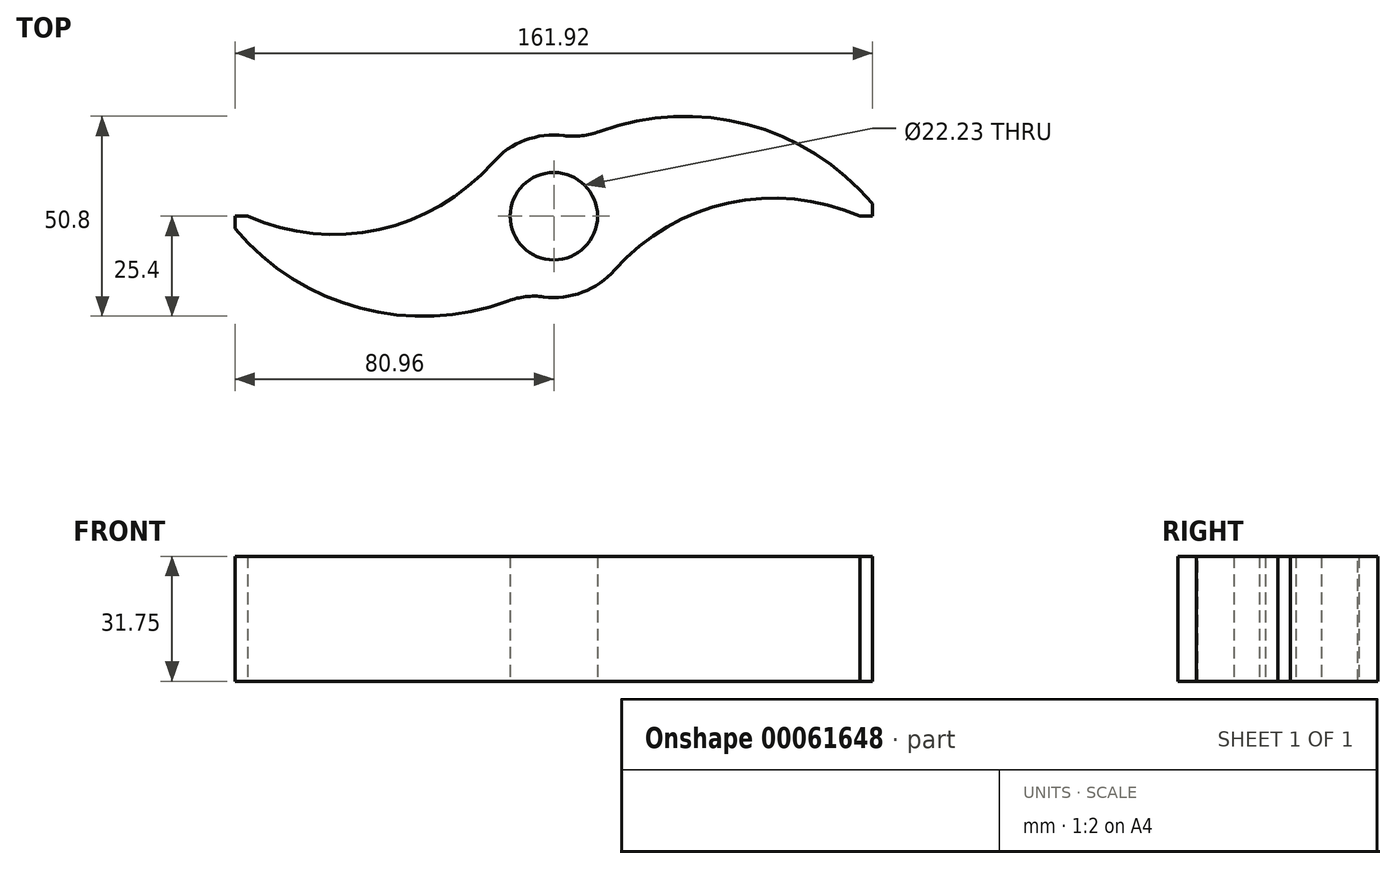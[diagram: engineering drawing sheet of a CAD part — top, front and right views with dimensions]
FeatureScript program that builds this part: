
annotation { "Feature Type Name" : "Feature", "Feature Type Description" : "" }
export const myFeature = defineFeature(function(context is Context, id is Id, definition is map)
    precondition{}
    {
        {
            var Q0;
            Q0=qCreatedBy(makeId("Top.planeOp"),FACE);
            var sketch = newSketch(context, id + "F0", { "sketchPlane" : qUnion([Q0])});
            skCircle(sketch, "E0", {"center": v(0, 0) * mm, "radius": 20.64 * mm});
            skLineSegment(sketch, "E1", {"start": v(0, 0) * mm, "end": v(80.96, 0) * mm, "construction": true});
            skLineSegment(sketch, "E2", {"start": v(0, 0) * mm, "end": v(-80.96, 0) * mm, "construction": true});
            skLineSegment(sketch, "E3.bottom", {"start": v(-80.96, 0) * mm, "end": v(-77.79, 0) * mm});
            skLineSegment(sketch, "E3.top", {"start": v(-80.96, -3.18) * mm, "end": v(-77.79, -3.18) * mm});
            skLineSegment(sketch, "E3.left", {"start": v(-80.96, 0) * mm, "end": v(-80.96, -3.18) * mm});
            skLineSegment(sketch, "E3.right", {"start": v(-77.79, 0) * mm, "end": v(-77.79, -3.18) * mm});
            skLineSegment(sketch, "E4.bottom", {"start": v(80.96, 0) * mm, "end": v(77.79, 0) * mm});
            skLineSegment(sketch, "E4.top", {"start": v(80.96, 3.18) * mm, "end": v(77.79, 3.17) * mm});
            skLineSegment(sketch, "E4.left", {"start": v(80.96, 0) * mm, "end": v(80.96, 3.18) * mm});
            skLineSegment(sketch, "E4.right", {"start": v(77.79, 0) * mm, "end": v(77.79, 3.17) * mm});
            skLineSegment(sketch, "E5", {"start": v(0, 25.4) * mm, "end": v(76.2, 25.4) * mm, "construction": true});
            skLineSegment(sketch, "E6", {"start": v(0, -25.4) * mm, "end": v(-76.2, -25.4) * mm, "construction": true});
            skArc(sketch, "E7", {"start": v(80.96, 3.17) * mm, "mid": v(46.64, 23.95) * mm, "end": v(6.78, 19.5) * mm});
            skArc(sketch, "E8", {"start": v(-80.96, -3.18) * mm, "mid": v(-46.64, -23.95) * mm, "end": v(-6.78, -19.5) * mm});
            skArc(sketch, "E9", {"start": v(-77.79, 0) * mm, "mid": v(-44.4, -3.36) * mm, "end": v(-15.48, 13.65) * mm});
            skArc(sketch, "E10", {"start": v(77.79, 0) * mm, "mid": v(44.4, 3.36) * mm, "end": v(15.48, -13.65) * mm});
            skSolve(sketch);
        }
        {
            var Q0;
            Q0 = qSketchRegion(id + "F0", true);
            extrude(context, id + "F1", {"entities" : qUnion([Q0]), "depth" : 31.75 * mm});
        }
        {
            var Q0;
            Q0=qCreatedBy(makeId("Top.planeOp"),FACE);
            var sketch = newSketch(context, id + "F2", { "sketchPlane" : qUnion([Q0])});
            skCircle(sketch, "E11", {"center": v(0, 0) * mm, "radius": 11.11 * mm});
            skSolve(sketch);
        }
        {
            var Q0;
            Q0 = qSketchRegion(id + "F2", true);
            extrude(context, id + "F3", {"entities" : qUnion([Q0]), "operationType" : NewBodyOperationType.REMOVE, "depth" : 31.75 * mm});
        }
        {
            var Q0;
            Q0=makeQuery(id+"F1.opExtrude","SWEPT_EDGE",EDGE,{"disambiguationData":[OSD([sQuery(id+"F0.wireOp",EDGE,"E0"),sQuery(id+"F0.wireOp",EDGE,"E8")])]});
            fillet(context, id + "F4", {"entities" : qUnion([Q0]), "radius" : 19.05 * mm, "tangentPropagation" : true, "allowEdgeOverflow" : false});
        }
        {
            var Q0;
            Q0=makeQuery(id+"F1.opExtrude","SWEPT_EDGE",EDGE,{"disambiguationData":[OSD([sQuery(id+"F0.wireOp",EDGE,"E0"),sQuery(id+"F0.wireOp",EDGE,"E7")])]});
            fillet(context, id + "F5", {"entities" : qUnion([Q0]), "radius" : 19.05 * mm, "tangentPropagation" : true, "allowEdgeOverflow" : false});
        }
    });
